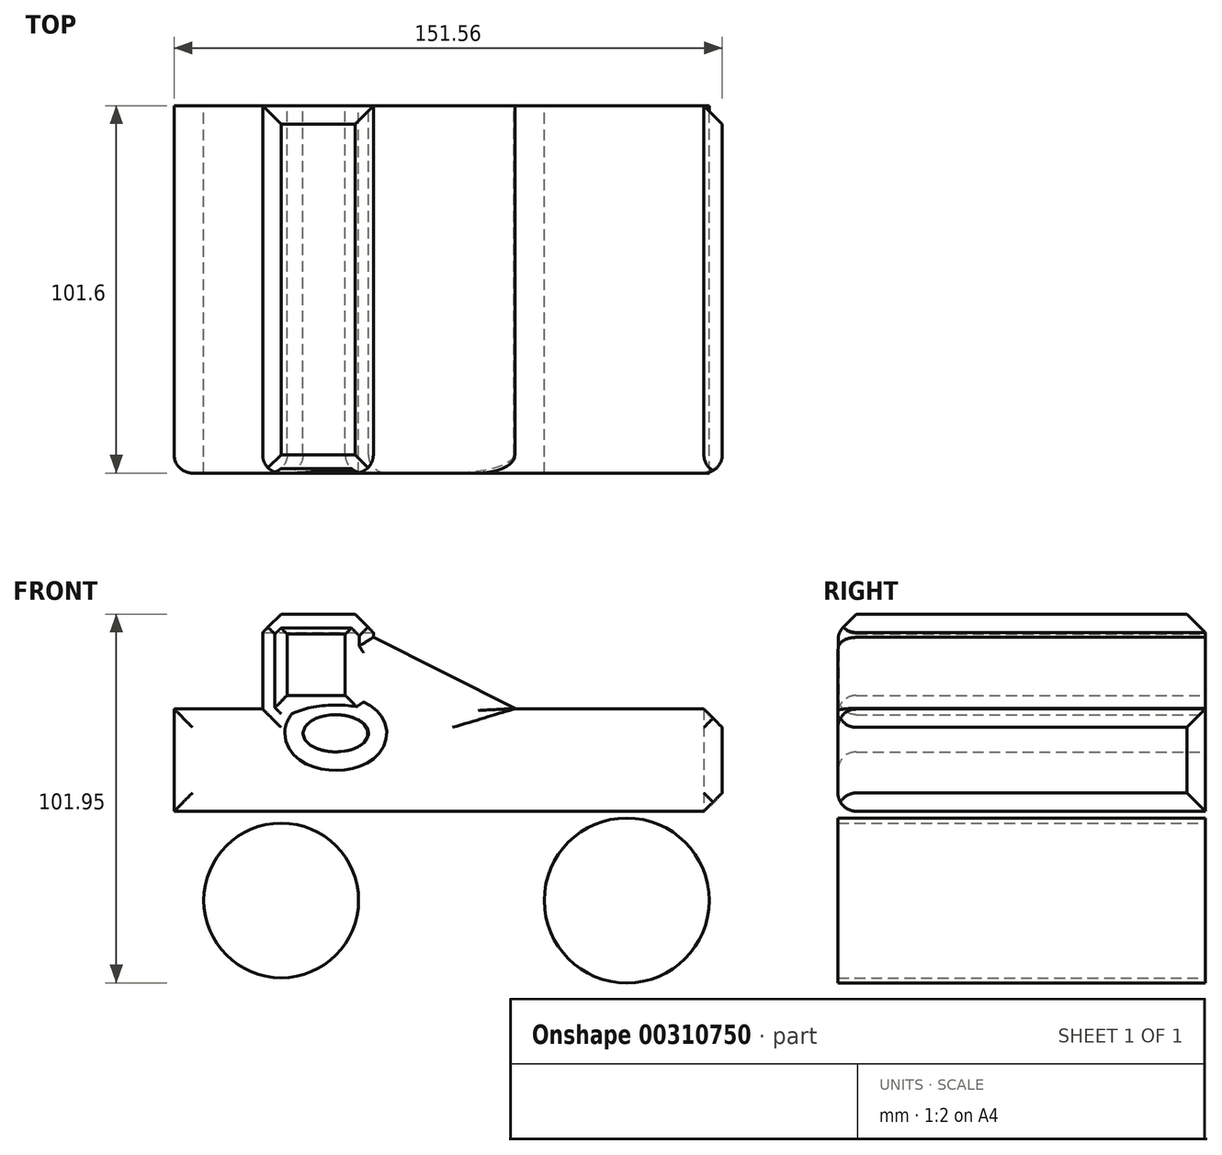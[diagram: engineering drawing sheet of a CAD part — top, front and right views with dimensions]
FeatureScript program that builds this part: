
annotation { "Feature Type Name" : "Feature", "Feature Type Description" : "" }
export const myFeature = defineFeature(function(context is Context, id is Id, definition is map)
    precondition{}
    {
        {
            var Q0;
            Q0=qCreatedBy(makeId("Front.planeOp"),FACE);
            var sketch = newSketch(context, id + "F0", { "sketchPlane" : qUnion([Q0])});
            skCircle(sketch, "E0", {"center": v(-40.95, -33.25) * mm, "radius": 21.4 * mm});
            skCircle(sketch, "E1", {"center": v(54.6, -33.25) * mm, "radius": 22.8 * mm});
            skLineSegment(sketch, "E2.bottom", {"start": v(-70.56, 19.67) * mm, "end": v(-46.08, 19.67) * mm});
            skLineSegment(sketch, "E2.top", {"start": v(-70.56, -8.6) * mm, "end": v(81, -8.6) * mm});
            skLineSegment(sketch, "E2.left", {"start": v(-70.56, 19.67) * mm, "end": v(-70.56, -8.6) * mm});
            skLineSegment(sketch, "E2.right", {"start": v(81, 19.67) * mm, "end": v(81, -8.6) * mm});
            skLineSegment(sketch, "E3.bottom", {"start": v(-17.57, 19.67) * mm, "end": v(-17.39, 19.67) * mm});
            skLineSegment(sketch, "E3.top", {"start": v(-46.08, 45.9) * mm, "end": v(-15.47, 45.9) * mm});
            skLineSegment(sketch, "E3.left", {"start": v(-46.08, 19.67) * mm, "end": v(-46.08, 45.9) * mm});
            skArc(sketch, "E4.cCircle", {"start": v(3.8, 6.8) * mm, "mid": v(3.39, 29.98) * mm, "end": v(-17.39, 19.67) * mm, "construction": true});
            skLineSegment(sketch, "E4.0", {"start": v(23.65, 19.85) * mm, "end": v(23.38, 19.67) * mm});
            skLineSegment(sketch, "E4.2", {"start": v(-15.47, 39.5) * mm, "end": v(23.65, 19.85) * mm});
            skPoint(sketch, "E4.0.midPoint", {"position": v(3.8, 6.8) * mm});
            skLineSegment(sketch, "E5.trimOffspring", {"start": v(-15.47, 39.5) * mm, "end": v(-15.47, 45.9) * mm});
            skPoint(sketch, "E6.orphan", {"position": v(-18.82, 41.18) * mm});
            skLineSegment(sketch, "E7.trimOffspring", {"start": v(23.38, 19.67) * mm, "end": v(81, 19.67) * mm});
            skPoint(sketch, "E8.trimOffspring.end.orphan", {"position": v(-16.06, -6.27) * mm});
            skLineSegment(sketch, "E9.bottom", {"start": v(-39.28, 40.37) * mm, "end": v(-23.25, 40.37) * mm});
            skLineSegment(sketch, "E9.top", {"start": v(-39.28, 23.46) * mm, "end": v(-23.25, 23.46) * mm});
            skLineSegment(sketch, "E9.left", {"start": v(-39.28, 40.37) * mm, "end": v(-39.28, 23.46) * mm});
            skLineSegment(sketch, "E9.right", {"start": v(-23.25, 40.37) * mm, "end": v(-23.25, 23.46) * mm});
            skEllipse(sketch, "E10", {"center": v(-25.87, 12.97) * mm, "majorRadius": 9.04 * mm, "minorRadius": 5.14 * mm, "majorAxis": v(-1, 0)});
            skSolve(sketch);
        }
        {
            var Q0;
            Q0=makeQuery(id+"F0.imprint","IMPRINT",FACE,{"disambiguationData":[TD([[makeQuery(id+"F0.imprint","IMPRINT",EDGE,{"derivedFrom":sQuery(id+"F0.wireOp",EDGE,"E2.bottom")}),-1.0]])]});
            var Q1;
            Q1=makeQuery(id+"F0.imprint","IMPRINT",FACE,{"disambiguationData":[TD([[makeQuery(id+"F0.imprint","IMPRINT",EDGE,{"derivedFrom":sQuery(id+"F0.wireOp",EDGE,"E0")}),1.0]])]});
            var Q2;
            Q2=makeQuery(id+"F0.imprint","IMPRINT",FACE,{"disambiguationData":[TD([[makeQuery(id+"F0.imprint","IMPRINT",EDGE,{"derivedFrom":sQuery(id+"F0.wireOp",EDGE,"E1")}),1.0]])]});
            extrude(context, id + "F1", {"entities" : qUnion([Q0, Q1, Q2]), "depth" : 101.6 * mm});
        }
        {
            var Q0;
            Q0=makeQuery(id+"F1.opExtrude","SWEPT_FACE",FACE,{"disambiguationData":[OSD([sQuery(id+"F0.wireOp",EDGE,"E3.top")])]});
            chamfer(context, id + "F2", {"entities" : qUnion([Q0]), "width" : 5.08 * mm, "tangentPropagation" : true});
        }
        {
            var Q0;
            Q0=makeQuery(id+"F1.opExtrude","CAP_FACE",FACE,{"disambiguationData":[OSD([sQuery(id+"F0.wireOp",EDGE,"E2.bottom"),sQuery(id+"F0.wireOp",EDGE,"E2.top"),sQuery(id+"F0.wireOp",EDGE,"E2.left"),sQuery(id+"F0.wireOp",EDGE,"E2.right"),sQuery(id+"F0.wireOp",EDGE,"E3.top"),sQuery(id+"F0.wireOp",EDGE,"E3.left"),sQuery(id+"F0.wireOp",EDGE,"E4.0"),sQuery(id+"F0.wireOp",EDGE,"E4.2"),sQuery(id+"F0.wireOp",EDGE,"E5.trimOffspring"),sQuery(id+"F0.wireOp",EDGE,"E7.trimOffspring"),sQuery(id+"F0.wireOp",EDGE,"E9.bottom"),sQuery(id+"F0.wireOp",EDGE,"E9.top"),sQuery(id+"F0.wireOp",EDGE,"E9.left"),sQuery(id+"F0.wireOp",EDGE,"E9.right"),sQuery(id+"F0.wireOp",EDGE,"E10")])],"isStart":false});
            fillet(context, id + "F3", {"entities" : qUnion([Q0]), "radius" : 5.08 * mm, "tangentPropagation" : true, "allowEdgeOverflow" : false});
        }
        {
            var Q0;
            Q0=makeQuery(id+"F1.opExtrude","SWEPT_FACE",FACE,{"disambiguationData":[OSD([sQuery(id+"F0.wireOp",EDGE,"E2.right")])]});
            chamfer(context, id + "F4", {"entities" : qUnion([Q0]), "width" : 5.08 * mm, "tangentPropagation" : true});
        }
    });
